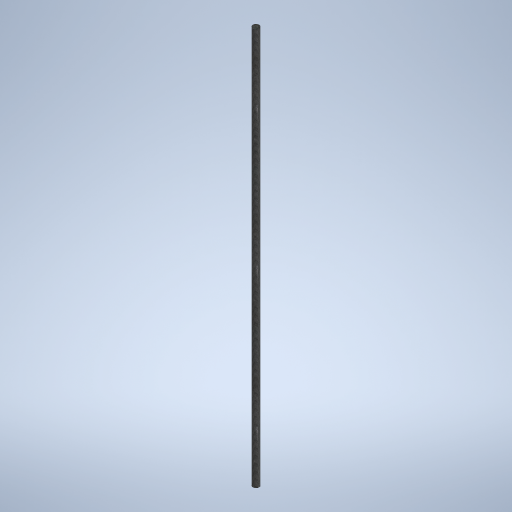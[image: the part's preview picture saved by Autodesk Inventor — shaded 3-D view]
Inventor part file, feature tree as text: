
AUTODESK INVENTOR PART (.ipt)
format: ipt  version: 2024 (Build 280153000, 153)  size: 247,296 bytes
history: native  units: mm
features: extrude x1, thread x1, sketch x1
ambient origin geometry x8: Origin, YZ Plane, XZ Plane, XY Plane, X Axis, Y Axis, Z Axis, Center Point
bodies: Solid1 (feature_tree)
feature tree (3):
  extrude  "Extrusion1"  Depth=500.0mm
  thread  "Thread1"  [1 undecoded]
  sketch  "Sketch1"  dims[d0=500.0mm d1=0.0mm d2=8.0mm d3=450.0mm d4=0.0mm]
note: 1 required parameter value undecoded (feature->parameter linkage not recoverable at this tier; creation-order binding heuristic only, values carry confidence <= 0.55)
